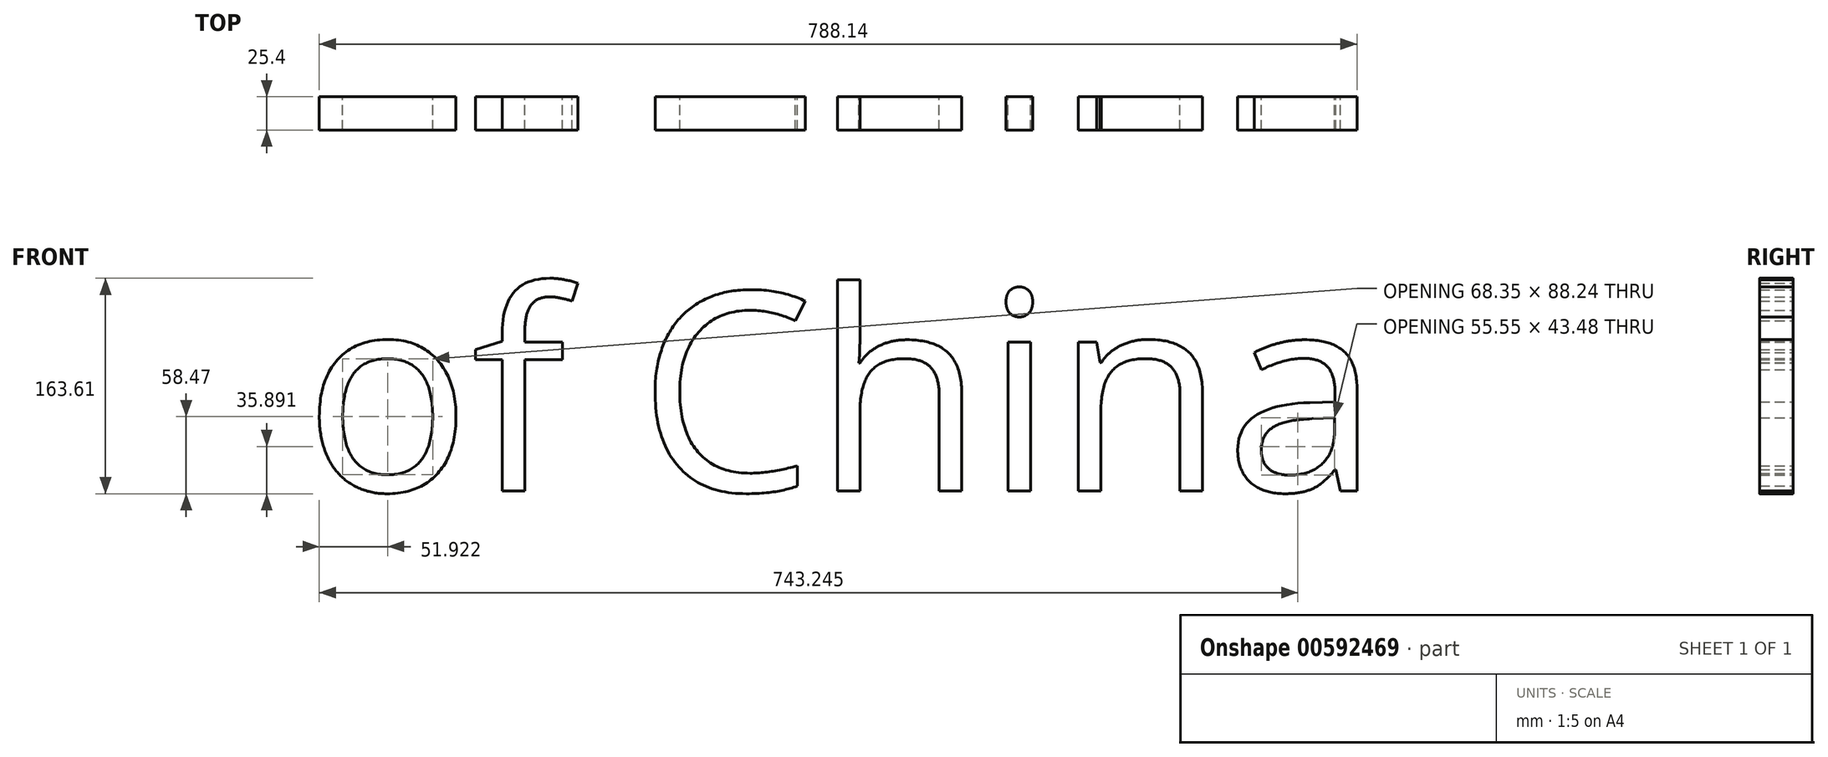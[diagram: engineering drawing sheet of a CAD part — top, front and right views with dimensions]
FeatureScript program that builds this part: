
annotation { "Feature Type Name" : "Feature", "Feature Type Description" : "" }
export const myFeature = defineFeature(function(context is Context, id is Id, definition is map)
    precondition{}
    {
        {
            var Q0;
            Q0=qCreatedBy(makeId("Front.planeOp"),FACE);
            var sketch = newSketch(context, id + "F0", { "sketchPlane" : qUnion([Q0])});
            skText(sketch, "E0", { "text": "of China", "fontName": "OpenSans-Regular.ttf"});
            const initialGuessF0  = {"E0": [-0.07516, -0.07533, 1, 0, 0.152]};
            skSetInitialGuess(sketch, initialGuessF0);
            skSolve(sketch);
        }
        {
            var Q0;
            Q0 = qSketchRegion(id + "F0", true);
            extrude(context, id + "F1", {"entities" : qUnion([Q0]), "depth" : 25.4 * mm, "offsetDistance" : 25.4 * mm});
        }
    });
